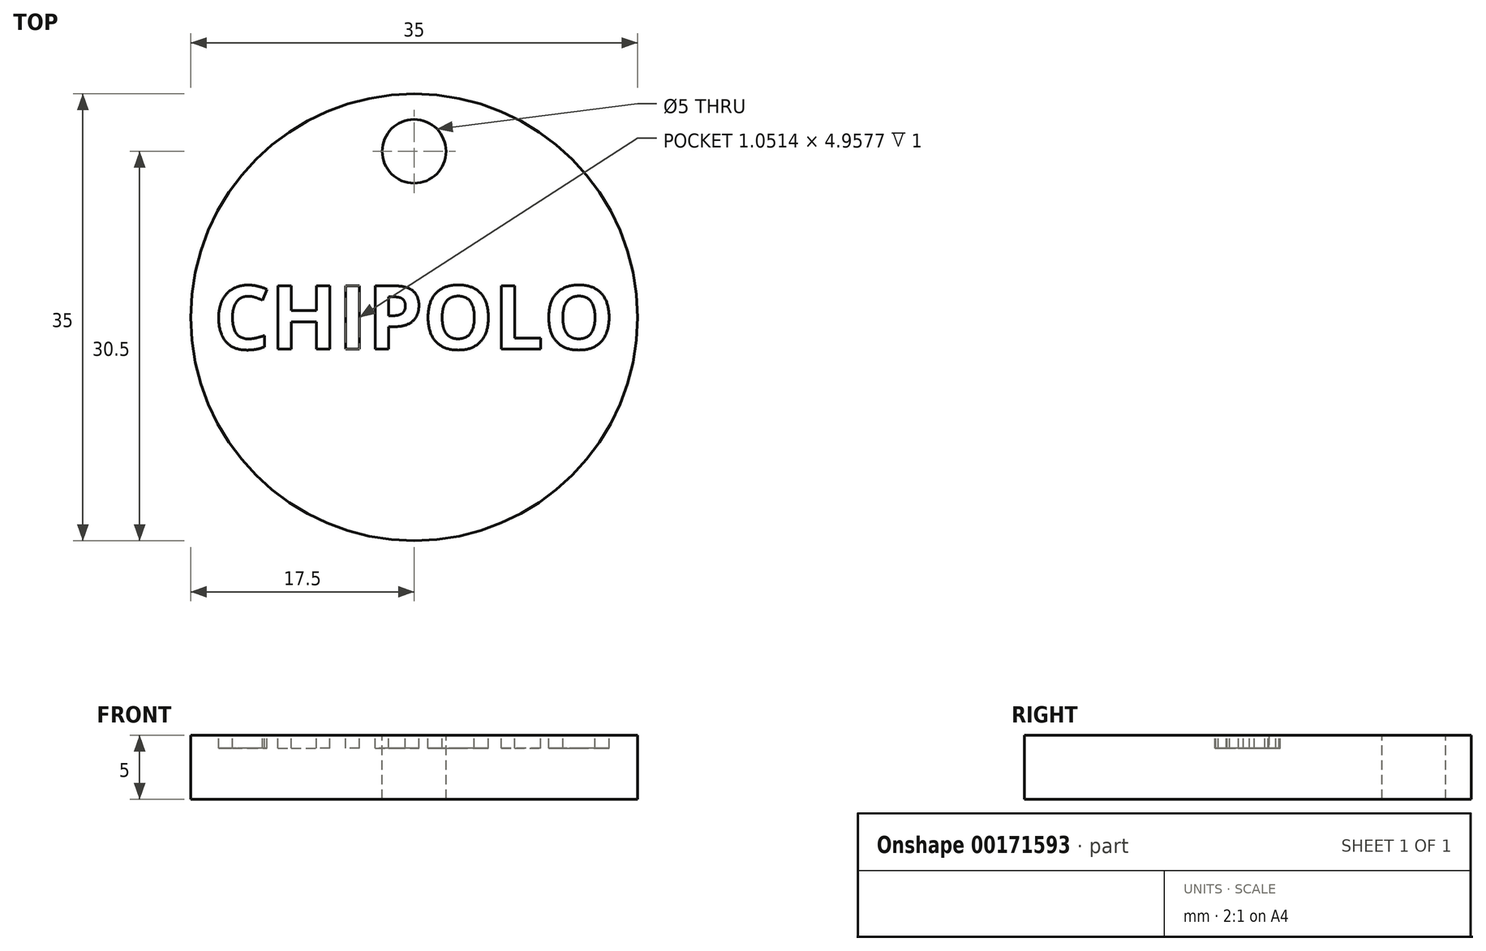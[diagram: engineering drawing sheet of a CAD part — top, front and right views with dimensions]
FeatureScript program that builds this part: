
annotation { "Feature Type Name" : "Feature", "Feature Type Description" : "" }
export const myFeature = defineFeature(function(context is Context, id is Id, definition is map)
    precondition{}
    {
        {
            var Q0;
            Q0=qCreatedBy(makeId("Top.planeOp"),FACE);
            var sketch = newSketch(context, id + "F0", { "sketchPlane" : qUnion([Q0])});
            skCircle(sketch, "E0", {"center": v(0, 0) * mm, "radius": 17.5 * mm});
            skSolve(sketch);
        }
        {
            var Q0;
            Q0 = qSketchRegion(id + "F0", true);
            extrude(context, id + "F1", {"entities" : qUnion([Q0]), "depth" : 5 * mm});
        }
        {
            var Q0;
            Q0=makeQuery(id+"F1.opExtrude","CAP_FACE",FACE,{"disambiguationData":[OSD([sQuery(id+"F0.wireOp",EDGE,"E0")])],"isStart":false});
            var sketch = newSketch(context, id + "F2", { "sketchPlane" : qUnion([Q0])});
            skText(sketch, "E1", { "text": "CHIPOLO", "fontName": "OpenSans-Bold.ttf"});
            const initialGuessF2  = {"E1": [-0.01571, -0.0025, 1, 0, 0.005]};
            skSetInitialGuess(sketch, initialGuessF2);
            skSolve(sketch);
        }
        {
            var Q0;
            Q0 = qSketchRegion(id + "F2", true);
            extrude(context, id + "F3", {"entities" : qUnion([Q0]), "operationType" : NewBodyOperationType.REMOVE, "oppositeDirection" : true, "depth" : 1 * mm});
        }
        {
            var Q0;
            {var subQ0=sQuery(id+"F0.wireOp",EDGE,"E0");Q0=makeQuery(id+"F3.boolean.opBoolean","SPLIT",FACE,{"disambiguationData":[TD([makeQuery(id+"F1.opExtrude","SWEPT_FACE",FACE,{"disambiguationData":[OSD([subQ0])]})])],"derivedFrom":makeQuery(id+"F1.opExtrude","CAP_FACE",FACE,{"disambiguationData":[OSD([subQ0])],"isStart":false})});}
            var sketch = newSketch(context, id + "F4", { "sketchPlane" : qUnion([Q0])});
            skCircle(sketch, "E2", {"center": v(0, 13) * mm, "radius": 2.5 * mm});
            skSolve(sketch);
        }
        {
            var Q0;
            Q0=makeQuery(id+"F4.imprint","IMPRINT",FACE,{"disambiguationData":[TD([[makeQuery(id+"F4.imprint","IMPRINT",EDGE,{"derivedFrom":sQuery(id+"F4.wireOp",EDGE,"E2")}),1.0]])]});
            extrude(context, id + "F5", {"entities" : qUnion([Q0]), "operationType" : NewBodyOperationType.REMOVE, "oppositeDirection" : true, "depth" : 25 * mm});
        }
    });
